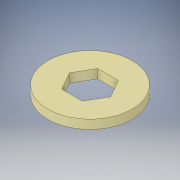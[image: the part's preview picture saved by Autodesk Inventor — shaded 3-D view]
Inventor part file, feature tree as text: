
AUTODESK INVENTOR PART (.ipt)
format: ipt  version: 2019 (Build 230136000, 136)  size: 116,736 bytes
history: native  units: mm
features: other x1, extrude x1, sketch x1
ambient origin geometry x8: Origin, YZ Plane, XZ Plane, XY Plane, X Axis, Y Axis, Z Axis, Center Point
bodies: Body1 (feature_tree)
feature tree (3):
  other  "Sólido1"
  extrude  "Extrusión1"  TaperAngle=0.0deg  [1 undecoded]
  sketch  "Boceto1"  dims[d0=12.8mm d1=0.0mm d2=30.0mm d3=3.18mm d4=0.0mm]
note: 1 required parameter value undecoded (feature->parameter linkage not recoverable at this tier; creation-order binding heuristic only, values carry confidence <= 0.55)
